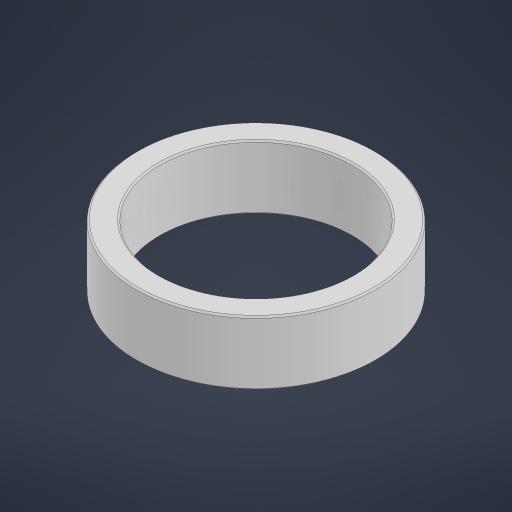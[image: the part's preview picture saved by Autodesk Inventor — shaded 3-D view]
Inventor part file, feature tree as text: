
AUTODESK INVENTOR PART (.ipt)
format: ipt  version: 2023 (Build 270158000, 158)  size: 186,880 bytes
history: native  units: in
note: dims shown in document units (in); Inventor stores cm internally (conversion verified against a paired STEP export)
features: chamfer x1
ambient origin geometry x8: Origin, YZ Plane, XZ Plane, XY Plane, X Axis, Y Axis, Z Axis, Center Point
bodies: Solid1 (feature_tree)
feature tree (1):
  chamfer  "Chamfer1"  [1 undecoded]
note: 1 required parameter value undecoded (feature->parameter linkage not recoverable at this tier; creation-order binding heuristic only, values carry confidence <= 0.55)
